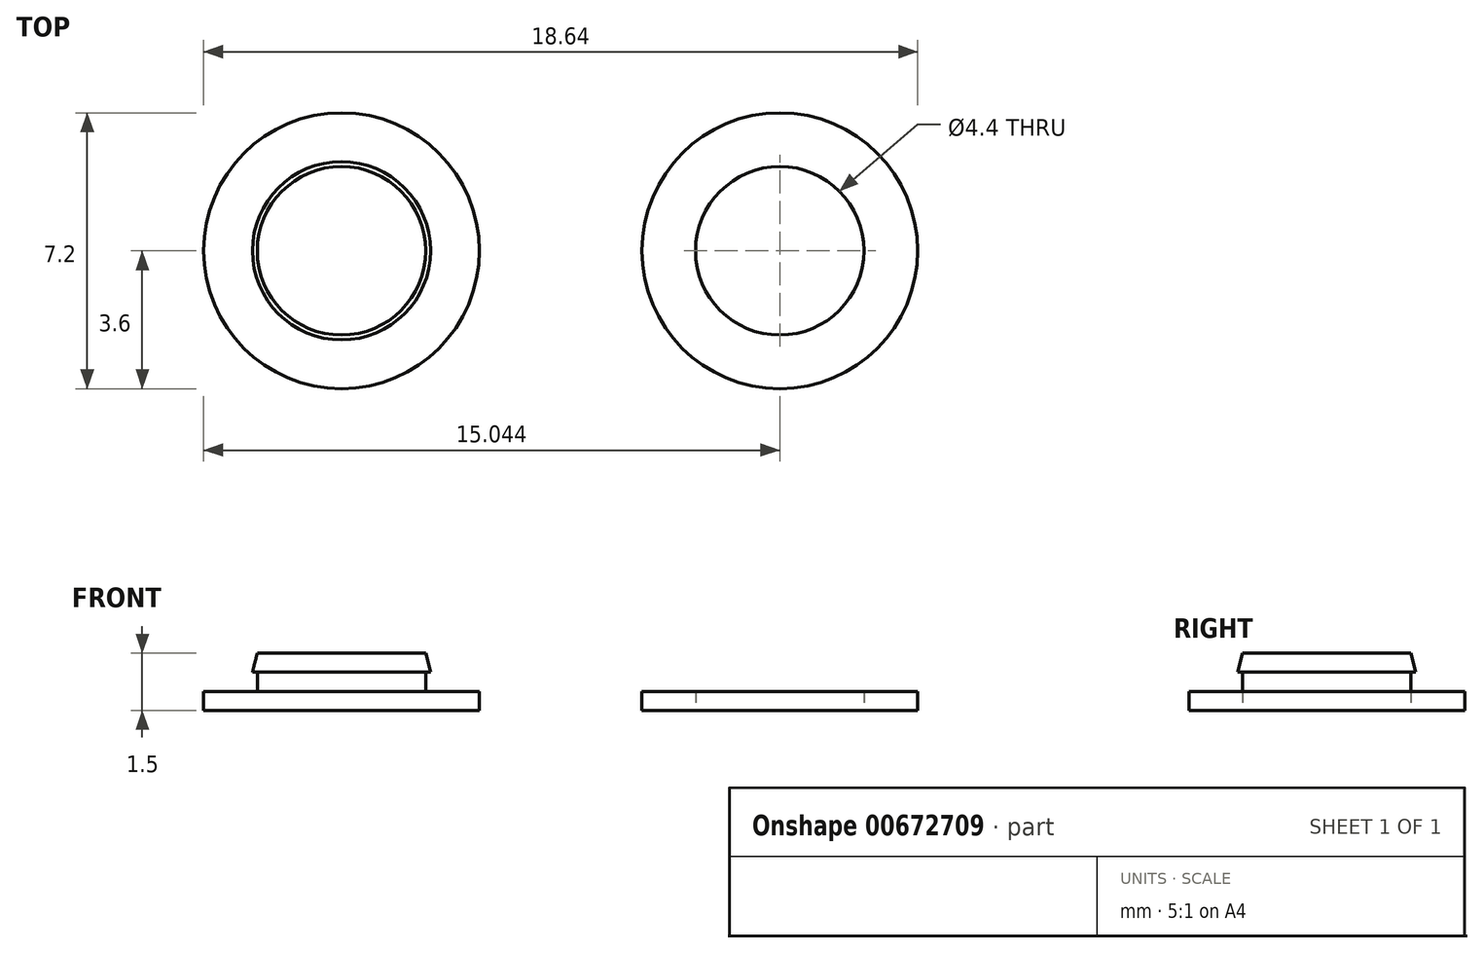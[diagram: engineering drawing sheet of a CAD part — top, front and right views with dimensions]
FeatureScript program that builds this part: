
annotation { "Feature Type Name" : "Feature", "Feature Type Description" : "" }
export const myFeature = defineFeature(function(context is Context, id is Id, definition is map)
    precondition{}
    {
        {
            var Q0;
            Q0=qCreatedBy(makeId("Front.planeOp"),FACE);
            var sketch = newSketch(context, id + "F0", { "sketchPlane" : qUnion([Q0])});
            skLineSegment(sketch, "E0.bottom", {"start": v(0, 0) * mm, "end": v(2.2, 0) * mm});
            skLineSegment(sketch, "E0.top", {"start": v(0, 1.5) * mm, "end": v(2.2, 1.5) * mm});
            skLineSegment(sketch, "E0.left", {"start": v(0, 0) * mm, "end": v(0, 1.5) * mm});
            skLineSegment(sketch, "E0.right", {"start": v(2.2, 0.5) * mm, "end": v(2.2, 1.5) * mm});
            skLineSegment(sketch, "E1.bottom", {"start": v(0, 0) * mm, "end": v(3.6, 0) * mm});
            skLineSegment(sketch, "E1.top", {"start": v(2.2, 0.5) * mm, "end": v(3.6, 0.5) * mm});
            skLineSegment(sketch, "E1.left", {"start": v(0, 0) * mm, "end": v(0, 0.5) * mm});
            skLineSegment(sketch, "E1.right", {"start": v(3.6, 0) * mm, "end": v(3.6, 0.5) * mm});
            skLineSegment(sketch, "E2", {"start": v(2.2, 1) * mm, "end": v(2.33, 1) * mm});
            skLineSegment(sketch, "E3", {"start": v(2.33, 1) * mm, "end": v(2.2, 1.5) * mm});
            skSolve(sketch);
        }
        {
            var Q0;
            {var subQ2=sQuery(id+"F0.wireOp",EDGE,"E2");Q0=makeQuery(id+"F0.imprint","IMPRINT",FACE,{"disambiguationData":[TD([[makeQuery(id+"F0.imprint","IMPRINT",EDGE,{"derivedFrom":subQ2}),1.0]])]});}
            var Q1;
            {var subQ1=sQuery(id+"F0.wireOp",EDGE,"E0.top");Q1=makeQuery(id+"F0.imprint","IMPRINT",FACE,{"disambiguationData":[TD([[makeQuery(id+"F0.imprint","IMPRINT",EDGE,{"derivedFrom":subQ1}),-1.0]])]});}
            var Q2;
            Q2=sQuery(id+"F0.wireOp",EDGE,"E0.left");
            revolve(context, id + "F1", {"entities" : qUnion([Q0, Q1]), "axis" : qUnion([Q2]), "revolveType" : RevolveType.FULL});
        }
        {
            var Q0;
            Q0=qCreatedBy(makeId("Top.planeOp"),FACE);
            var sketch = newSketch(context, id + "F2", { "sketchPlane" : qUnion([Q0])});
            skCircle(sketch, "E4", {"center": v(11.44, 0) * mm, "radius": 3.6 * mm});
            skCircle(sketch, "E5", {"center": v(11.44, 0) * mm, "radius": 2.2 * mm});
            skSolve(sketch);
        }
        {
            var Q0;
            Q0=makeQuery(id+"F2.imprint","IMPRINT",FACE,{"disambiguationData":[TD([[makeQuery(id+"F2.imprint","IMPRINT",EDGE,{"derivedFrom":sQuery(id+"F2.wireOp",EDGE,"E4")}),1.0]])]});
            extrude(context, id + "F3", {"entities" : qUnion([Q0]), "depth" : .5 * mm, "offsetDistance" : 25 * mm});
        }
    });
